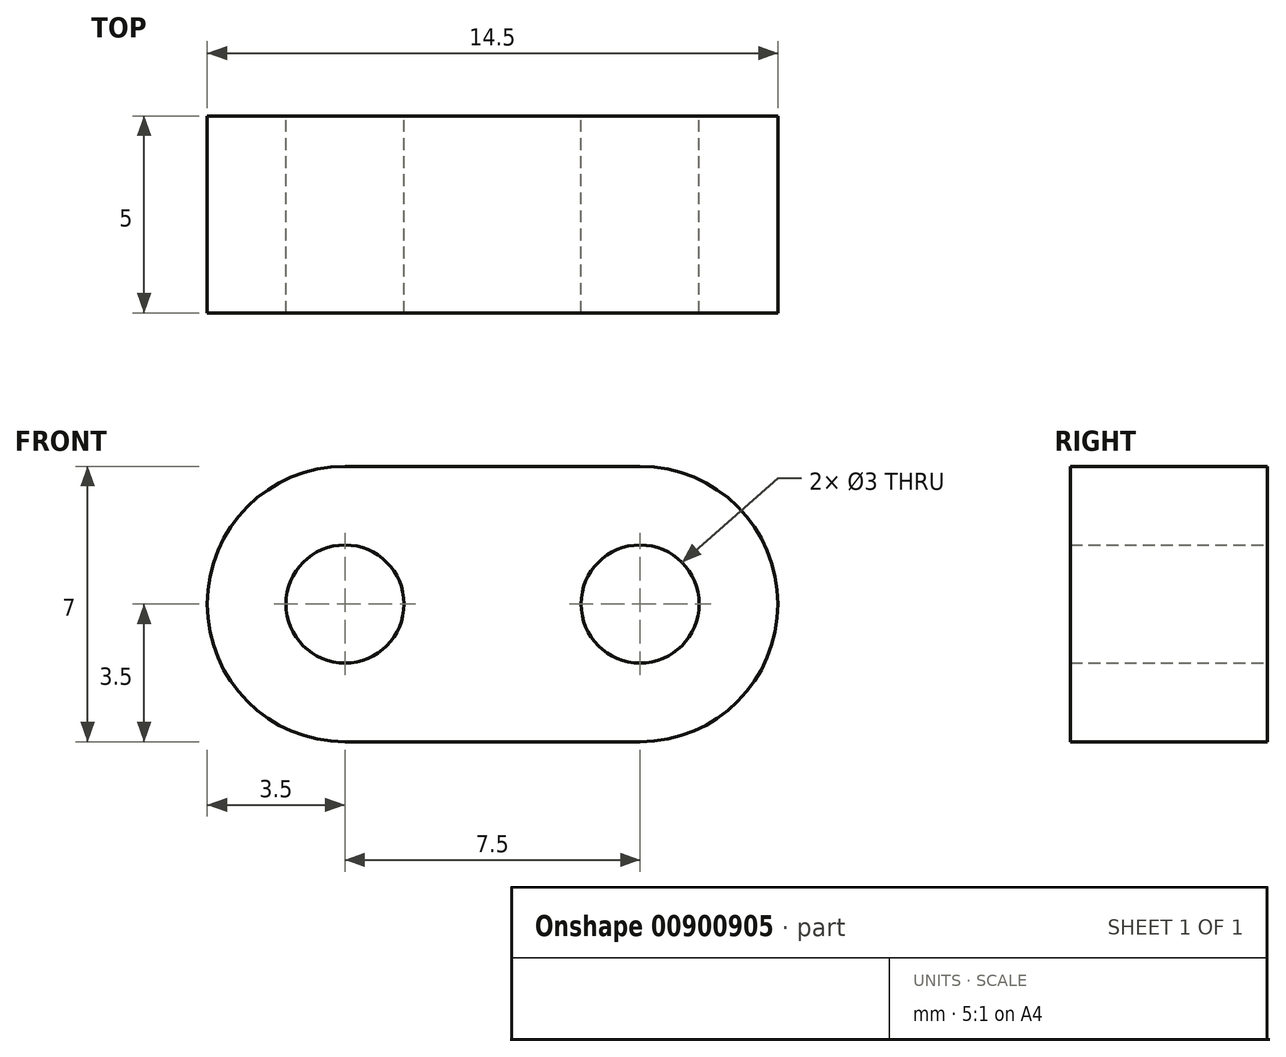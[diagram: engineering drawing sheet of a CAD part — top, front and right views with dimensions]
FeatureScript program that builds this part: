
annotation { "Feature Type Name" : "Feature", "Feature Type Description" : "" }
export const myFeature = defineFeature(function(context is Context, id is Id, definition is map)
    precondition{}
    {
        {
            var Q0;
            Q0=qCreatedBy(makeId("Front.planeOp"),FACE);
            var sketch = newSketch(context, id + "F0", { "sketchPlane" : qUnion([Q0])});
            skArc(sketch, "E0", {"start": v(-3.75, 3.5) * mm, "mid": v(-7.25, 0) * mm, "end": v(-3.75, -3.5) * mm});
            skArc(sketch, "E1", {"start": v(3.75, -3.5) * mm, "mid": v(7.25, 0) * mm, "end": v(3.75, 3.5) * mm});
            skCircle(sketch, "E2", {"center": v(-3.75, 0) * mm, "radius": 1.5 * mm});
            skCircle(sketch, "E3", {"center": v(3.75, 0) * mm, "radius": 1.5 * mm});
            skLineSegment(sketch, "E4", {"start": v(-3.75, 3.5) * mm, "end": v(3.75, 3.5) * mm});
            skLineSegment(sketch, "E5", {"start": v(-3.75, -3.5) * mm, "end": v(3.75, -3.5) * mm});
            skSolve(sketch);
        }
        {
            var Q0;
            Q0 = qSketchRegion(id + "F0", true);
            extrude(context, id + "F1", {"entities" : qUnion([Q0]), "endBound" : BoundingType.SYMMETRIC, "depth" : 5 * mm, "offsetDistance" : 25 * mm});
        }
    });
